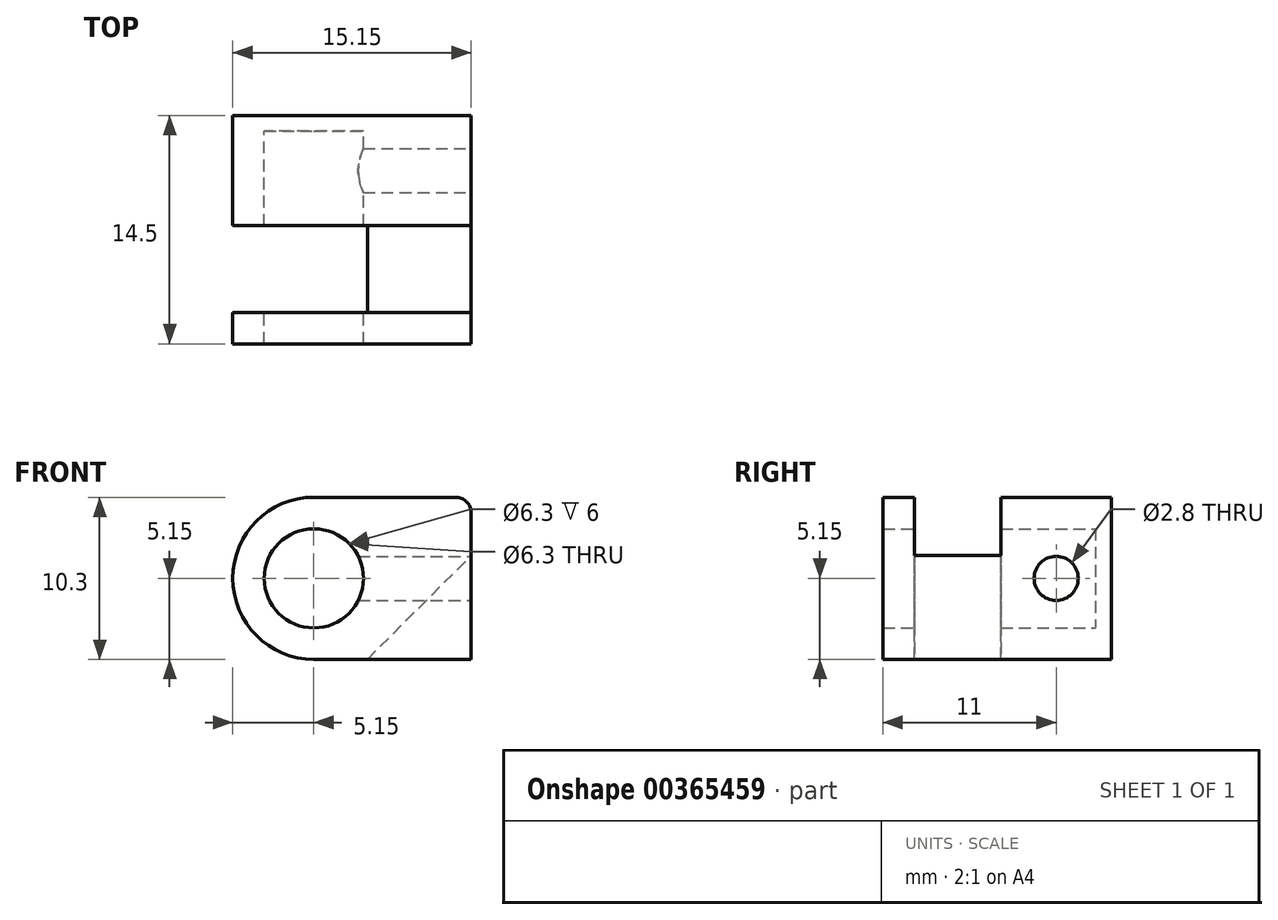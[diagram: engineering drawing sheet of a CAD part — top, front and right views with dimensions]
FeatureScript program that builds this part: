
annotation { "Feature Type Name" : "Feature", "Feature Type Description" : "" }
export const myFeature = defineFeature(function(context is Context, id is Id, definition is map)
    precondition{}
    {
        {
            var Q0;
            Q0=qCreatedBy(makeId("Front.planeOp"),FACE);
            var sketch = newSketch(context, id + "F0", { "sketchPlane" : qUnion([Q0])});
            skCircle(sketch, "E0", {"center": v(0, 0) * mm, "radius": 3.15 * mm});
            skArc(sketch, "E1", {"start": v(0, 5.15) * mm, "mid": v(-5.15, 0) * mm, "end": v(0, -5.15) * mm});
            skLineSegment(sketch, "E2", {"start": v(0, 0) * mm, "end": v(0, 5.15) * mm});
            skLineSegment(sketch, "E3", {"start": v(10, 0) * mm, "end": v(10, 5.15) * mm});
            skLineSegment(sketch, "E4", {"start": v(10, 5.15) * mm, "end": v(0, 5.15) * mm});
            skLineSegment(sketch, "E5", {"start": v(0, 0) * mm, "end": v(0, -5.15) * mm});
            skLineSegment(sketch, "E6", {"start": v(0, -5.15) * mm, "end": v(10, -5.15) * mm});
            skLineSegment(sketch, "E7", {"start": v(10, -5.15) * mm, "end": v(10, 0) * mm});
            skSolve(sketch);
        }
        {
            var Q0;
            Q0 = qSketchRegion(id + "F0", true);
            extrude(context, id + "F1", {"entities" : qUnion([Q0]), "depth" : 14.5 * mm});
        }
        {
            var Q0;
            Q0=makeQuery(id+"F1.opExtrude","CAP_FACE",FACE,{"disambiguationData":[OSD([sQuery(id+"F0.wireOp",EDGE,"E0"),sQuery(id+"F0.wireOp",EDGE,"E1"),sQuery(id+"F0.wireOp",EDGE,"E3"),sQuery(id+"F0.wireOp",EDGE,"E4"),sQuery(id+"F0.wireOp",EDGE,"E6"),sQuery(id+"F0.wireOp",EDGE,"E7")])],"isStart":false});
            cPlane(context, id + "F2", {"entities" : qUnion([Q0]), "cplaneType" : CPlaneType.OFFSET, "offset" : 2 * mm, "oppositeDirection" : true, "width" : 150 * mm, "height" : 150 * mm});
        }
        {
            var Q0;
            Q0=qCreatedBy(id+"F2.planeOp",FACE);
            var sketch = newSketch(context, id + "F3", { "sketchPlane" : qUnion([Q0])});
            skLineSegment(sketch, "E8", {"start": v(0, -5.15) * mm, "end": v(3.4, -5.15) * mm});
            skLineSegment(sketch, "E9", {"start": v(3.4, -5.15) * mm, "end": v(10, 1.45) * mm});
            skLineSegment(sketch, "E10", {"start": v(3.4, -5.15) * mm, "end": v(-9.8, -5.15) * mm});
            skLineSegment(sketch, "E11", {"start": v(-9.8, -5.15) * mm, "end": v(-9.8, 5.73) * mm});
            skLineSegment(sketch, "E12", {"start": v(-9.8, 5.73) * mm, "end": v(10, 5.73) * mm});
            skLineSegment(sketch, "E13", {"start": v(10, 5.73) * mm, "end": v(10, 1.45) * mm});
            skSolve(sketch);
        }
        {
            var Q0;
            Q0 = qSketchRegion(id + "F3", true);
            extrude(context, id + "F4", {"entities" : qUnion([Q0]), "operationType" : NewBodyOperationType.REMOVE, "oppositeDirection" : true, "depth" : 5.5 * mm});
        }
        {
            var Q0;
            Q0=makeQuery(id+"F1.opExtrude","SWEPT_FACE",FACE,{"disambiguationData":[OSD([sQuery(id+"F0.wireOp",EDGE,"E3"),sQuery(id+"F0.wireOp",EDGE,"E7")])]});
            var sketch = newSketch(context, id + "F5", { "sketchPlane" : qUnion([Q0])});
            skCircle(sketch, "E14", {"center": v(-3.5, 0) * mm, "radius": 1.4 * mm});
            skPoint(sketch, "E14.centerSnap0", {"position": v(-3.5, 5.15) * mm});
            skPoint(sketch, "E14.centerSnap1", {"position": v(0, 0) * mm});
            skSolve(sketch);
        }
        {
            var Q0;
            Q0 = qSketchRegion(id + "F5", true);
            extrude(context, id + "F6", {"entities" : qUnion([Q0]), "operationType" : NewBodyOperationType.REMOVE, "oppositeDirection" : true, "depth" : 9.5 * mm});
        }
        {
            var Q0;
            Q0=makeQuery(id+"F1.opExtrude","CAP_FACE",FACE,{"disambiguationData":[OSD([sQuery(id+"F0.wireOp",EDGE,"E0"),sQuery(id+"F0.wireOp",EDGE,"E1"),sQuery(id+"F0.wireOp",EDGE,"E3"),sQuery(id+"F0.wireOp",EDGE,"E4"),sQuery(id+"F0.wireOp",EDGE,"E6"),sQuery(id+"F0.wireOp",EDGE,"E7")])],"isStart":true});
            var sketch = newSketch(context, id + "F7", { "sketchPlane" : qUnion([Q0])});
            skCircle(sketch, "E15", {"center": v(0, 0) * mm, "radius": 4 * mm});
            skSolve(sketch);
        }
        {
            var Q0;
            Q0 = qSketchRegion(id + "F7", true);
            extrude(context, id + "F8", {"entities" : qUnion([Q0]), "operationType" : NewBodyOperationType.ADD, "oppositeDirection" : true, "depth" : 1 * mm});
        }
        {
            var Q0;
            {var subQ1=sQuery(id+"F0.wireOp",EDGE,"E4");var subQ2=sQuery(id+"F0.wireOp",EDGE,"E3");Q0=makeQuery(id+"F4.boolean.opBoolean","SPLIT",EDGE,{"disambiguationData":[TD([makeQuery(id+"F4.opExtrude","CAP_FACE",FACE,{"disambiguationData":[OSD([sQuery(id+"F3.wireOp",EDGE,"E9"),sQuery(id+"F3.wireOp",EDGE,"E10"),sQuery(id+"F3.wireOp",EDGE,"E11"),sQuery(id+"F3.wireOp",EDGE,"E12"),sQuery(id+"F3.wireOp",EDGE,"E13")])],"isStart":true})])],"derivedFrom":makeQuery(id+"F1.opExtrude","SWEPT_EDGE",EDGE,{"disambiguationData":[OSD([subQ2,subQ1])]})});}
            var Q1;
            {var subQ1=sQuery(id+"F0.wireOp",EDGE,"E4");var subQ2=sQuery(id+"F0.wireOp",EDGE,"E3");Q1=makeQuery(id+"F4.boolean.opBoolean","SPLIT",EDGE,{"disambiguationData":[TD([makeQuery(id+"F4.opExtrude","CAP_FACE",FACE,{"disambiguationData":[OSD([sQuery(id+"F3.wireOp",EDGE,"E9"),sQuery(id+"F3.wireOp",EDGE,"E10"),sQuery(id+"F3.wireOp",EDGE,"E11"),sQuery(id+"F3.wireOp",EDGE,"E12"),sQuery(id+"F3.wireOp",EDGE,"E13")])],"isStart":false})])],"derivedFrom":makeQuery(id+"F1.opExtrude","SWEPT_EDGE",EDGE,{"disambiguationData":[OSD([subQ2,subQ1])]})});}
            fillet(context, id + "F9", {"entities" : qUnion([Q0, Q1]), "radius" : 1 * mm, "tangentPropagation" : true, "allowEdgeOverflow" : false});
        }
    });
